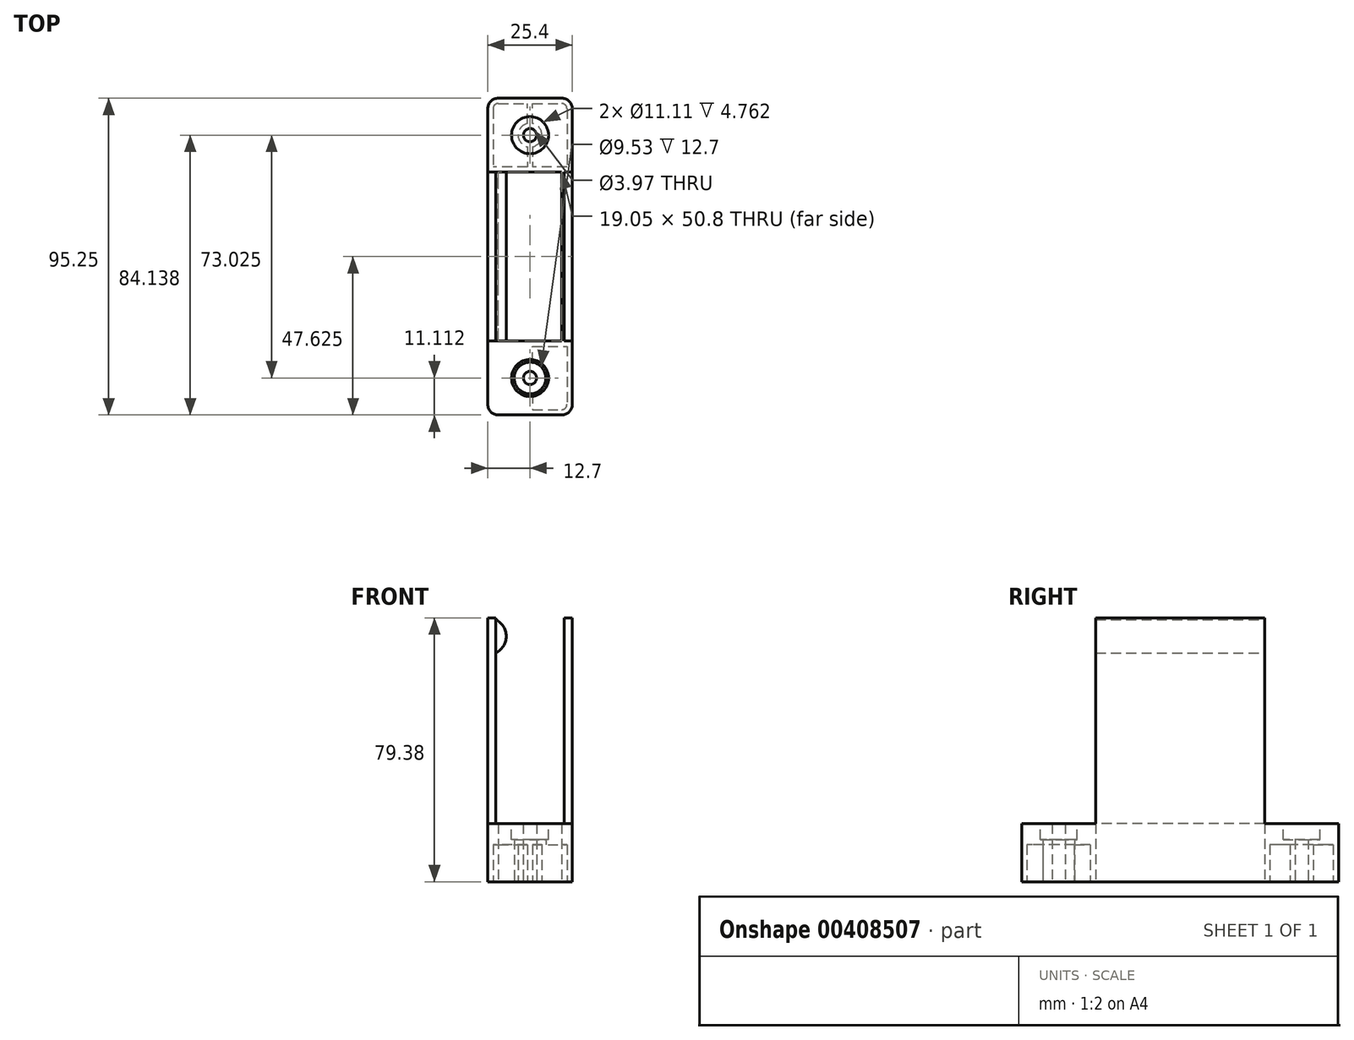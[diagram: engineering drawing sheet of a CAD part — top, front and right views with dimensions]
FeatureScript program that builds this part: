
annotation { "Feature Type Name" : "Feature", "Feature Type Description" : "" }
export const myFeature = defineFeature(function(context is Context, id is Id, definition is map)
    precondition{}
    {
        {
            var Q0;
            Q0=qCreatedBy(makeId("Top.planeOp"),FACE);
            var sketch = newSketch(context, id + "F0", { "sketchPlane" : qUnion([Q0])});
            skLineSegment(sketch, "E0.bottom", {"start": v(3.18, 0) * mm, "end": v(22.23, 0) * mm});
            skLineSegment(sketch, "E0.top", {"start": v(3.18, -95.25) * mm, "end": v(22.23, -95.25) * mm});
            skLineSegment(sketch, "E0.left", {"start": v(0, -3.17) * mm, "end": v(0, -92.08) * mm});
            skLineSegment(sketch, "E0.right", {"start": v(25.4, -3.17) * mm, "end": v(25.4, -92.08) * mm});
            skPoint(sketch, "E1.visualSharp", {"position": v(0, 0) * mm});
            skArc(sketch, "E1.filletArc", {"start": v(3.18, 0) * mm, "mid": v(0.93, -0.93) * mm, "end": v(0, -3.18) * mm});
            skPoint(sketch, "E2.visualSharp", {"position": v(0, -95.25) * mm});
            skArc(sketch, "E2.filletArc", {"start": v(0, -92.08) * mm, "mid": v(0.93, -94.32) * mm, "end": v(3.18, -95.25) * mm});
            skPoint(sketch, "E3.visualSharp", {"position": v(25.4, -95.25) * mm});
            skArc(sketch, "E3.filletArc", {"start": v(22.23, -95.25) * mm, "mid": v(24.47, -94.32) * mm, "end": v(25.4, -92.08) * mm});
            skPoint(sketch, "E4.visualSharp", {"position": v(25.4, 0) * mm});
            skArc(sketch, "E4.filletArc", {"start": v(25.4, -3.17) * mm, "mid": v(24.47, -0.93) * mm, "end": v(22.23, 0) * mm});
            skLineSegment(sketch, "E5", {"start": v(0, -47.63) * mm, "end": v(25.4, -47.62) * mm, "construction": true});
            skPoint(sketch, "E6", {"position": v(12.7, -47.62) * mm});
            skLineSegment(sketch, "E7", {"start": v(12.7, 0) * mm, "end": v(12.7, -95.25) * mm, "construction": true});
            skLineSegment(sketch, "E8", {"start": v(12.7, -22.23) * mm, "end": v(22.23, -22.23) * mm});
            skLineSegment(sketch, "E9", {"start": v(22.23, -22.23) * mm, "end": v(22.23, -47.62) * mm});
            skLineSegment(sketch, "E10.MirrorCS", {"start": v(22.23, -73.02) * mm, "end": v(22.23, -47.62) * mm});
            skLineSegment(sketch, "E11.MirrorCS", {"start": v(12.7, -73.02) * mm, "end": v(22.23, -73.02) * mm});
            skLineSegment(sketch, "E12.MirrorCS", {"start": v(12.7, -22.23) * mm, "end": v(3.18, -22.23) * mm});
            skLineSegment(sketch, "E13.MirrorCS", {"start": v(3.18, -22.22) * mm, "end": v(3.18, -47.62) * mm});
            skLineSegment(sketch, "E14.MirrorCS", {"start": v(3.17, -73.02) * mm, "end": v(3.18, -47.62) * mm});
            skLineSegment(sketch, "E15.MirrorCS", {"start": v(12.7, -73.02) * mm, "end": v(3.17, -73.02) * mm});
            skPoint(sketch, "E16.center.orphan", {"position": v(12.7, -11.11) * mm});
            skSolve(sketch);
        }
        {
            var Q0;
            Q0=makeQuery(id+"F0.imprint","IMPRINT",FACE,{"disambiguationData":[TD([[makeQuery(id+"F0.imprint","IMPRINT",EDGE,{"derivedFrom":sQuery(id+"F0.wireOp",EDGE,"E0.bottom")}),-1.0]])]});
            extrude(context, id + "F1", {"entities" : qUnion([Q0]), "depth" : 17.46 * mm});
        }
        {
            var Q0;
            Q0=makeQuery(id+"F1.opExtrude","CAP_FACE",FACE,{"disambiguationData":[OSD([sQuery(id+"F0.wireOp",EDGE,"E0.bottom"),sQuery(id+"F0.wireOp",EDGE,"E0.top"),sQuery(id+"F0.wireOp",EDGE,"E0.left"),sQuery(id+"F0.wireOp",EDGE,"E0.right"),sQuery(id+"F0.wireOp",EDGE,"E1.filletArc"),sQuery(id+"F0.wireOp",EDGE,"E2.filletArc"),sQuery(id+"F0.wireOp",EDGE,"E3.filletArc"),sQuery(id+"F0.wireOp",EDGE,"E4.filletArc")])],"isStart":false});
            var sketch = newSketch(context, id + "F2", { "sketchPlane" : qUnion([Q0])});
            skPoint(sketch, "E17.visualSharp", {"position": v(31.75, 0) * mm});
            skLineSegment(sketch, "E18", {"start": v(0, -47.62) * mm, "end": v(25.4, -47.62) * mm, "construction": true});
            skLineSegment(sketch, "E19", {"start": v(2.38, -22.22) * mm, "end": v(2.38, -47.62) * mm});
            skLineSegment(sketch, "E20", {"start": v(2.38, -22.22) * mm, "end": v(0, -22.22) * mm});
            skLineSegment(sketch, "E21", {"start": v(0, -22.22) * mm, "end": v(0, -47.62) * mm});
            skLineSegment(sketch, "E22.MirrorCS", {"start": v(2.38, -73.02) * mm, "end": v(0, -73.02) * mm});
            skLineSegment(sketch, "E23.MirrorCS", {"start": v(2.38, -73.02) * mm, "end": v(2.38, -47.62) * mm});
            skLineSegment(sketch, "E24.MirrorCS", {"start": v(0, -73.02) * mm, "end": v(0, -47.62) * mm});
            skLineSegment(sketch, "E25", {"start": v(12.7, 0) * mm, "end": v(12.7, -95.25) * mm, "construction": true});
            skLineSegment(sketch, "E26.MirrorCS", {"start": v(23.02, -22.22) * mm, "end": v(25.4, -22.22) * mm});
            skLineSegment(sketch, "E27.MirrorCS", {"start": v(23.02, -22.22) * mm, "end": v(23.02, -47.62) * mm});
            skLineSegment(sketch, "E28.MirrorCS", {"start": v(23.02, -73.02) * mm, "end": v(23.02, -47.62) * mm});
            skLineSegment(sketch, "E29.MirrorCS", {"start": v(23.02, -73.02) * mm, "end": v(25.4, -73.02) * mm});
            skLineSegment(sketch, "E30.MirrorCS", {"start": v(25.4, -73.02) * mm, "end": v(25.4, -47.62) * mm});
            skLineSegment(sketch, "E31.MirrorCS", {"start": v(25.4, -22.22) * mm, "end": v(25.4, -47.62) * mm});
            skSolve(sketch);
        }
        {
            var Q0;
            Q0=makeQuery(id+"F2.imprint","IMPRINT",FACE,{"disambiguationData":[TD([[makeQuery(id+"F2.imprint","IMPRINT",EDGE,{"derivedFrom":sQuery(id+"F2.wireOp",EDGE,"E19")}),-1.0]])]});
            var Q1;
            Q1=makeQuery(id+"F2.imprint","IMPRINT",FACE,{"disambiguationData":[TD([[makeQuery(id+"F2.imprint","IMPRINT",EDGE,{"derivedFrom":sQuery(id+"F2.wireOp",EDGE,"E26.MirrorCS")}),-1.0]])]});
            extrude(context, id + "F3", {"entities" : qUnion([Q0, Q1]), "operationType" : NewBodyOperationType.ADD, "depth" : 61.9 * mm});
        }
        {
            var Q0;
            Q0=makeQuery(id+"F1.opExtrude","CAP_FACE",FACE,{"disambiguationData":[OSD([sQuery(id+"F0.wireOp",EDGE,"E0.bottom"),sQuery(id+"F0.wireOp",EDGE,"E0.top"),sQuery(id+"F0.wireOp",EDGE,"E0.left"),sQuery(id+"F0.wireOp",EDGE,"E0.right"),sQuery(id+"F0.wireOp",EDGE,"E1.filletArc"),sQuery(id+"F0.wireOp",EDGE,"E2.filletArc"),sQuery(id+"F0.wireOp",EDGE,"E3.filletArc"),sQuery(id+"F0.wireOp",EDGE,"E4.filletArc")])],"isStart":true});
            var sketch = newSketch(context, id + "F4", { "sketchPlane" : qUnion([Q0])});
            skLineSegment(sketch, "E32", {"start": v(12.7, 0) * mm, "end": v(12.7, 95.25) * mm, "construction": true});
            skCircle(sketch, "E33", {"center": v(12.7, 11.11) * mm, "radius": 1.98 * mm});
            skLineSegment(sketch, "E34", {"start": v(0, 47.62) * mm, "end": v(25.4, 47.62) * mm, "construction": true});
            skCircle(sketch, "E35.MirrorC", {"center": v(12.7, 84.14) * mm, "radius": 1.98 * mm});
            skCircle(sketch, "E36", {"center": v(12.7, 84.14) * mm, "radius": 4.76 * mm});
            skCircle(sketch, "E37.MirrorC", {"center": v(12.7, 11.11) * mm, "radius": 4.76 * mm});
            skSolve(sketch);
        }
        {
            var Q0;
            Q0=makeQuery(id+"F4.imprint","IMPRINT",FACE,{"disambiguationData":[TD([[makeQuery(id+"F4.imprint","IMPRINT",EDGE,{"derivedFrom":sQuery(id+"F4.wireOp",EDGE,"E33")}),1.0]])]});
            var Q1;
            Q1=makeQuery(id+"F4.imprint","IMPRINT",FACE,{"disambiguationData":[TD([[makeQuery(id+"F4.imprint","IMPRINT",EDGE,{"derivedFrom":sQuery(id+"F4.wireOp",EDGE,"E35.MirrorC")}),-1.0]])]});
            var Q2;
            Q2=sQuery(id+"F4.wireOp",EDGE,"E33");
            var Q3;
            Q3=sQuery(id+"F4.wireOp",EDGE,"E35.MirrorC");
            extrude(context, id + "F5", {"entities" : qUnion([Q0, Q1]), "operationType" : NewBodyOperationType.REMOVE, "surfaceEntities" : qUnion([Q2, Q3]), "endBound" : BoundingType.THROUGH_ALL, "oppositeDirection" : true, "depth" : 25.4 * mm});
        }
        {
            var Q0;
            Q0=makeQuery(id+"F3.opExtrude","SWEPT_FACE",FACE,{"disambiguationData":[OSD([sQuery(id+"F2.wireOp",EDGE,"E20")])]});
            var sketch = newSketch(context, id + "F6", { "sketchPlane" : qUnion([Q0])});
            skArc(sketch, "E38", {"start": v(-2.38, 78.83) * mm, "mid": v(-5.56, 73.81) * mm, "end": v(-2.38, 68.8) * mm});
            skLineSegment(sketch, "E39", {"start": v(-2.38, 78.83) * mm, "end": v(-2.38, 68.8) * mm});
            skLineSegment(sketch, "E40", {"start": v(0, 73.81) * mm, "end": v(-25.4, 73.81) * mm, "construction": true});
            skLineSegment(sketch, "E41", {"start": v(-12.7, 73.81) * mm, "end": v(-12.7, 17.83) * mm, "construction": true});
            skArc(sketch, "E42.MirrorCS", {"start": v(-23.02, 78.83) * mm, "mid": v(-19.84, 73.81) * mm, "end": v(-23.02, 68.8) * mm});
            skLineSegment(sketch, "E43", {"start": v(-23.02, 68.8) * mm, "end": v(-23.02, 78.83) * mm});
            skPoint(sketch, "E44", {"position": v(-5.56, 73.81) * mm});
            skPoint(sketch, "E45", {"position": v(-19.84, 73.81) * mm});
            skSolve(sketch);
        }
        {
            var Q0;
            Q0=makeQuery(id+"F6.imprint","IMPRINT",FACE,{"disambiguationData":[TD([[makeQuery(id+"F6.imprint","IMPRINT",EDGE,{"derivedFrom":sQuery(id+"F6.wireOp",EDGE,"E42.MirrorCS")}),-1.0]])]});
            var Q1;
            Q1=makeQuery(id+"F6.imprint","IMPRINT",FACE,{"disambiguationData":[TD([[makeQuery(id+"F6.imprint","IMPRINT",EDGE,{"derivedFrom":sQuery(id+"F6.wireOp",EDGE,"E38")}),1.0]])]});
            extrude(context, id + "F7", {"entities" : qUnion([Q0, Q1]), "oppositeDirection" : true, "depth" : 50.8 * mm});
        }
        {
            var Q0;
            Q0=makeQuery(id+"F0.imprint","IMPRINT",FACE,{"disambiguationData":[TD([[makeQuery(id+"F0.imprint","IMPRINT",EDGE,{"derivedFrom":sQuery(id+"F0.wireOp",EDGE,"E8")}),-1.0]])]});
            extrude(context, id + "F8", {"entities" : qUnion([Q0]), "operationType" : NewBodyOperationType.REMOVE, "depth" : 3.17 * mm});
        }
        {
            var Q0;
            Q0=makeQuery(id+"F1.opExtrude","CAP_FACE",FACE,{"disambiguationData":[OSD([sQuery(id+"F0.wireOp",EDGE,"E0.bottom"),sQuery(id+"F0.wireOp",EDGE,"E0.top"),sQuery(id+"F0.wireOp",EDGE,"E0.left"),sQuery(id+"F0.wireOp",EDGE,"E0.right"),sQuery(id+"F0.wireOp",EDGE,"E1.filletArc"),sQuery(id+"F0.wireOp",EDGE,"E2.filletArc"),sQuery(id+"F0.wireOp",EDGE,"E3.filletArc"),sQuery(id+"F0.wireOp",EDGE,"E4.filletArc"),sQuery(id+"F0.wireOp",EDGE,"E8"),sQuery(id+"F0.wireOp",EDGE,"E9"),sQuery(id+"F0.wireOp",EDGE,"E10.MirrorCS"),sQuery(id+"F0.wireOp",EDGE,"E11.MirrorCS"),sQuery(id+"F0.wireOp",EDGE,"E12.MirrorCS"),sQuery(id+"F0.wireOp",EDGE,"E13.MirrorCS"),sQuery(id+"F0.wireOp",EDGE,"E14.MirrorCS"),sQuery(id+"F0.wireOp",EDGE,"E15.MirrorCS")])],"isStart":true});
            var sketch = newSketch(context, id + "F9", { "sketchPlane" : qUnion([Q0])});
            skLineSegment(sketch, "E46", {"start": v(0, 39.8) * mm, "end": v(0, 49.47) * mm, "construction": true});
            skLineSegment(sketch, "E47", {"start": v(0, 47.62) * mm, "end": v(25.4, 47.62) * mm, "construction": true});
            skArc(sketch, "E48", {"start": v(11.9, 87.62) * mm, "mid": v(9.13, 84.14) * mm, "end": v(11.9, 80.65) * mm});
            skLineSegment(sketch, "E49", {"start": v(12.7, 47.62) * mm, "end": v(12.7, 95.25) * mm, "construction": true});
            skLineSegment(sketch, "E50.0", {"start": v(3.18, 93.66) * mm, "end": v(22.22, 93.66) * mm});
            skLineSegment(sketch, "E50.1", {"start": v(1.59, 3.18) * mm, "end": v(1.59, 92.08) * mm});
            skLineSegment(sketch, "E50.2", {"start": v(3.18, 1.59) * mm, "end": v(22.22, 1.59) * mm});
            skLineSegment(sketch, "E50.3", {"start": v(23.81, 3.18) * mm, "end": v(23.81, 92.08) * mm});
            skPoint(sketch, "E51.visualSharp", {"position": v(23.81, 93.66) * mm});
            skArc(sketch, "E51.filletArc", {"start": v(23.81, 92.08) * mm, "mid": v(23.35, 93.2) * mm, "end": v(22.22, 93.66) * mm});
            skPoint(sketch, "E52.visualSharp", {"position": v(1.59, 93.66) * mm});
            skArc(sketch, "E52.filletArc", {"start": v(3.18, 93.66) * mm, "mid": v(2.05, 93.2) * mm, "end": v(1.59, 92.08) * mm});
            skPoint(sketch, "E53.visualSharp", {"position": v(1.59, 1.59) * mm});
            skArc(sketch, "E53.filletArc", {"start": v(1.59, 3.18) * mm, "mid": v(2.05, 2.05) * mm, "end": v(3.18, 1.59) * mm});
            skPoint(sketch, "E54.visualSharp", {"position": v(23.81, 1.59) * mm});
            skArc(sketch, "E54.filletArc", {"start": v(22.22, 1.59) * mm, "mid": v(23.35, 2.05) * mm, "end": v(23.81, 3.18) * mm});
            skLineSegment(sketch, "E55", {"start": v(11.9, 87.62) * mm, "end": v(11.9, 93.66) * mm});
            skLineSegment(sketch, "E56.MirrorCS", {"start": v(13.5, 87.62) * mm, "end": v(13.5, 93.66) * mm});
            skLineSegment(sketch, "E57", {"start": v(11.9, 80.65) * mm, "end": v(11.9, 74.61) * mm});
            skLineSegment(sketch, "E58.MirrorCS", {"start": v(13.5, 80.65) * mm, "end": v(13.5, 74.61) * mm});
            skArc(sketch, "E59.trimOffspring", {"start": v(13.5, 80.65) * mm, "mid": v(16.27, 84.14) * mm, "end": v(13.5, 87.62) * mm});
            skPoint(sketch, "E60.MirrorCS.end.orphan", {"position": v(13.5, 1.59) * mm});
            skPoint(sketch, "E60.MirrorCS.start.orphan", {"position": v(13.5, 7.63) * mm});
            skPoint(sketch, "E61.MirrorCS.end.orphan", {"position": v(11.9, 1.59) * mm});
            skPoint(sketch, "E61.MirrorCS.start.orphan", {"position": v(11.9, 7.63) * mm});
            skLineSegment(sketch, "E62.MirrorCS", {"start": v(11.9, 7.63) * mm, "end": v(11.9, 1.59) * mm});
            skLineSegment(sketch, "E63.MirrorCS", {"start": v(13.5, 7.63) * mm, "end": v(13.5, 1.59) * mm});
            skArc(sketch, "E64.MirrorCS", {"start": v(11.9, 7.63) * mm, "mid": v(9.13, 11.11) * mm, "end": v(11.9, 14.6) * mm});
            skArc(sketch, "E65.MirrorCS", {"start": v(13.5, 14.6) * mm, "mid": v(16.27, 11.11) * mm, "end": v(13.5, 7.63) * mm});
            skLineSegment(sketch, "E66.MirrorCS", {"start": v(11.9, 14.6) * mm, "end": v(11.9, 20.64) * mm});
            skLineSegment(sketch, "E67.MirrorCS", {"start": v(13.5, 14.6) * mm, "end": v(13.5, 20.64) * mm});
            skLineSegment(sketch, "E68.0", {"start": v(1.59, 74.61) * mm, "end": v(11.9, 74.61) * mm});
            skLineSegment(sketch, "E68.1", {"start": v(1.59, 74.61) * mm, "end": v(1.59, 20.64) * mm});
            skLineSegment(sketch, "E68.2", {"start": v(23.81, 20.64) * mm, "end": v(13.5, 20.64) * mm});
            skLineSegment(sketch, "E68.3", {"start": v(23.81, 20.64) * mm, "end": v(23.81, 74.61) * mm});
            skLineSegment(sketch, "E69.trimOffspring", {"start": v(13.5, 74.61) * mm, "end": v(23.81, 74.61) * mm});
            skPoint(sketch, "E70.orphan", {"position": v(13.5, 73.02) * mm});
            skPoint(sketch, "E71.orphan", {"position": v(11.9, 73.02) * mm});
            skPoint(sketch, "E72.orphan", {"position": v(11.9, 22.22) * mm});
            skLineSegment(sketch, "E73.trimOffspring", {"start": v(11.9, 20.64) * mm, "end": v(1.59, 20.64) * mm});
            skPoint(sketch, "E74.orphan", {"position": v(13.5, 22.22) * mm});
            skSolve(sketch);
        }
        {
            var Q0;
            Q0=makeQuery(id+"F9.imprint","IMPRINT",FACE,{"disambiguationData":[TD([[makeQuery(id+"F9.imprint","IMPRINT",EDGE,{"derivedFrom":makeQuery(id+"F5.boolean.opBoolean","COPY",EDGE,{"derivedFrom":makeQuery(id+"F5.opExtrude","CAP_EDGE",EDGE,{"disambiguationData":[OSD([sQuery(id+"F4.wireOp",EDGE,"E33")])],"isStart":true})})}),1.0]])]});
            var Q1;
            Q1=makeQuery(id+"F9.imprint","IMPRINT",FACE,{"disambiguationData":[TD([[makeQuery(id+"F9.imprint","IMPRINT",EDGE,{"derivedFrom":makeQuery(id+"F5.boolean.opBoolean","COPY",EDGE,{"derivedFrom":makeQuery(id+"F5.opExtrude","CAP_EDGE",EDGE,{"disambiguationData":[OSD([sQuery(id+"F4.wireOp",EDGE,"E35.MirrorC")])],"isStart":true})})}),-1.0]])]});
            var Q2;
            Q2=makeQuery(id+"F9.imprint","IMPRINT",FACE,{"disambiguationData":[TD([[makeQuery(id+"F9.imprint","IMPRINT",EDGE,{"derivedFrom":sQuery(id+"F9.wireOp",EDGE,"E50.3")}),1.0]])]});
            var Q3;
            Q3=makeQuery(id+"F9.imprint","IMPRINT",FACE,{"disambiguationData":[TD([[makeQuery(id+"F9.imprint","IMPRINT",EDGE,{"derivedFrom":sQuery(id+"F9.wireOp",EDGE,"E48")}),-1.0]])]});
            var Q4;
            {var subQ2=sQuery(id+"F9.wireOp",EDGE,"E53.filletArc");Q4=makeQuery(id+"F9.imprint","IMPRINT",FACE,{"disambiguationData":[TD([[makeQuery(id+"F9.imprint","IMPRINT",EDGE,{"derivedFrom":subQ2}),1.0]])]});}
            extrude(context, id + "F10", {"entities" : qUnion([Q0, Q1, Q2, Q3, Q4]), "operationType" : NewBodyOperationType.REMOVE, "oppositeDirection" : true, "depth" : 11.1 * mm});
        }
        {
            var Q0;
            Q0=makeQuery(id+"F1.opExtrude","CAP_FACE",FACE,{"disambiguationData":[OSD([sQuery(id+"F0.wireOp",EDGE,"E0.bottom"),sQuery(id+"F0.wireOp",EDGE,"E0.top"),sQuery(id+"F0.wireOp",EDGE,"E0.left"),sQuery(id+"F0.wireOp",EDGE,"E0.right"),sQuery(id+"F0.wireOp",EDGE,"E1.filletArc"),sQuery(id+"F0.wireOp",EDGE,"E2.filletArc"),sQuery(id+"F0.wireOp",EDGE,"E3.filletArc"),sQuery(id+"F0.wireOp",EDGE,"E4.filletArc"),sQuery(id+"F0.wireOp",EDGE,"E8"),sQuery(id+"F0.wireOp",EDGE,"E9"),sQuery(id+"F0.wireOp",EDGE,"E10.MirrorCS"),sQuery(id+"F0.wireOp",EDGE,"E11.MirrorCS"),sQuery(id+"F0.wireOp",EDGE,"E12.MirrorCS"),sQuery(id+"F0.wireOp",EDGE,"E13.MirrorCS"),sQuery(id+"F0.wireOp",EDGE,"E14.MirrorCS"),sQuery(id+"F0.wireOp",EDGE,"E15.MirrorCS")])],"isStart":false});
            var sketch = newSketch(context, id + "F11", { "sketchPlane" : qUnion([Q0])});
            skCircle(sketch, "E75", {"center": v(12.7, -11.11) * mm, "radius": 5.56 * mm});
            skCircle(sketch, "E76", {"center": v(12.7, -84.14) * mm, "radius": 5.56 * mm});
            skSolve(sketch);
        }
        {
            var Q0;
            Q0=makeQuery(id+"F11.imprint","IMPRINT",FACE,{"disambiguationData":[TD([[makeQuery(id+"F11.imprint","IMPRINT",EDGE,{"derivedFrom":makeQuery(id+"F5.boolean.opBoolean","INTERSECT",EDGE,{"derivedFrom":[makeQuery(id+"F1.opExtrude","CAP_FACE",FACE,{"disambiguationData":[OSD([sQuery(id+"F0.wireOp",EDGE,"E0.bottom"),sQuery(id+"F0.wireOp",EDGE,"E0.top"),sQuery(id+"F0.wireOp",EDGE,"E0.left"),sQuery(id+"F0.wireOp",EDGE,"E0.right"),sQuery(id+"F0.wireOp",EDGE,"E1.filletArc"),sQuery(id+"F0.wireOp",EDGE,"E2.filletArc"),sQuery(id+"F0.wireOp",EDGE,"E3.filletArc"),sQuery(id+"F0.wireOp",EDGE,"E4.filletArc"),sQuery(id+"F0.wireOp",EDGE,"E8"),sQuery(id+"F0.wireOp",EDGE,"E9"),sQuery(id+"F0.wireOp",EDGE,"E10.MirrorCS"),sQuery(id+"F0.wireOp",EDGE,"E11.MirrorCS"),sQuery(id+"F0.wireOp",EDGE,"E12.MirrorCS"),sQuery(id+"F0.wireOp",EDGE,"E13.MirrorCS"),sQuery(id+"F0.wireOp",EDGE,"E14.MirrorCS"),sQuery(id+"F0.wireOp",EDGE,"E15.MirrorCS")])],"isStart":false}),makeQuery(id+"F5.opExtrude","SWEPT_FACE",FACE,{"disambiguationData":[OSD([sQuery(id+"F4.wireOp",EDGE,"E33")])]})]})}),1.0]])]});
            var Q1;
            Q1=makeQuery(id+"F11.imprint","IMPRINT",FACE,{"disambiguationData":[TD([[makeQuery(id+"F11.imprint","IMPRINT",EDGE,{"derivedFrom":makeQuery(id+"F5.boolean.opBoolean","INTERSECT",EDGE,{"derivedFrom":[makeQuery(id+"F1.opExtrude","CAP_FACE",FACE,{"disambiguationData":[OSD([sQuery(id+"F0.wireOp",EDGE,"E0.bottom"),sQuery(id+"F0.wireOp",EDGE,"E0.top"),sQuery(id+"F0.wireOp",EDGE,"E0.left"),sQuery(id+"F0.wireOp",EDGE,"E0.right"),sQuery(id+"F0.wireOp",EDGE,"E1.filletArc"),sQuery(id+"F0.wireOp",EDGE,"E2.filletArc"),sQuery(id+"F0.wireOp",EDGE,"E3.filletArc"),sQuery(id+"F0.wireOp",EDGE,"E4.filletArc"),sQuery(id+"F0.wireOp",EDGE,"E8"),sQuery(id+"F0.wireOp",EDGE,"E9"),sQuery(id+"F0.wireOp",EDGE,"E10.MirrorCS"),sQuery(id+"F0.wireOp",EDGE,"E11.MirrorCS"),sQuery(id+"F0.wireOp",EDGE,"E12.MirrorCS"),sQuery(id+"F0.wireOp",EDGE,"E13.MirrorCS"),sQuery(id+"F0.wireOp",EDGE,"E14.MirrorCS"),sQuery(id+"F0.wireOp",EDGE,"E15.MirrorCS")])],"isStart":false}),makeQuery(id+"F5.opExtrude","SWEPT_FACE",FACE,{"disambiguationData":[OSD([sQuery(id+"F4.wireOp",EDGE,"E35.MirrorC")])]})]})}),-1.0]])]});
            var Q2;
            Q2=makeQuery(id+"F11.imprint","IMPRINT",FACE,{"disambiguationData":[TD([[makeQuery(id+"F11.imprint","IMPRINT",EDGE,{"derivedFrom":sQuery(id+"F11.wireOp",EDGE,"E76")}),1.0]])]});
            var Q3;
            Q3=makeQuery(id+"F11.imprint","IMPRINT",FACE,{"disambiguationData":[TD([[makeQuery(id+"F11.imprint","IMPRINT",EDGE,{"derivedFrom":sQuery(id+"F11.wireOp",EDGE,"E75")}),1.0]])]});
            extrude(context, id + "F12", {"entities" : qUnion([Q0, Q1, Q2, Q3]), "operationType" : NewBodyOperationType.REMOVE, "oppositeDirection" : true, "depth" : 4.76 * mm});
        }
    });
